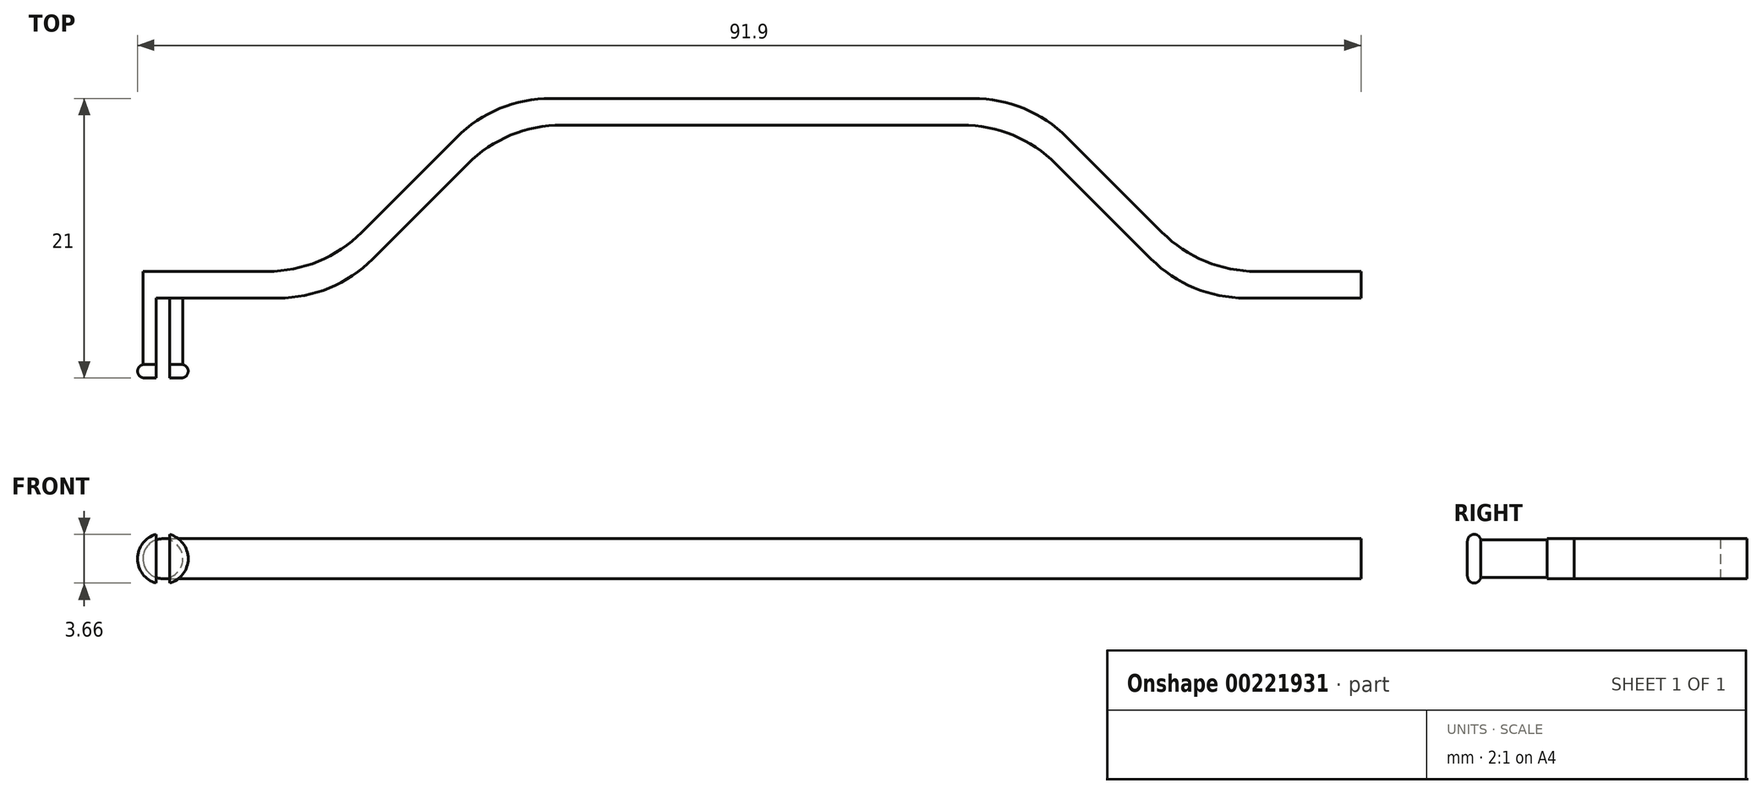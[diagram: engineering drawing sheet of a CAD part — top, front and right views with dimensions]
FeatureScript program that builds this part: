
annotation { "Feature Type Name" : "Feature", "Feature Type Description" : "" }
export const myFeature = defineFeature(function(context is Context, id is Id, definition is map)
    precondition{}
    {
        {
            var Q0;
            Q0=qCreatedBy(makeId("Top.planeOp"),FACE);
            var sketch = newSketch(context, id + "F0", { "sketchPlane" : qUnion([Q0])});
            skLineSegment(sketch, "E0.bottom", {"start": v(-45, 0) * mm, "end": v(-32.17, 0) * mm});
            skLineSegment(sketch, "E0.top", {"start": v(-45, 2) * mm, "end": v(-33, 2) * mm});
            skLineSegment(sketch, "E0.left", {"start": v(-45, 0) * mm, "end": v(-45, 2) * mm});
            skLineSegment(sketch, "E0.right", {"start": v(-32.17, 0) * mm, "end": v(-33, 2) * mm});
            skLineSegment(sketch, "E1.MirrorCS", {"start": v(32.17, 0) * mm, "end": v(33, 2) * mm});
            skLineSegment(sketch, "E2.MirrorCS", {"start": v(45, 0) * mm, "end": v(45, 2) * mm});
            skLineSegment(sketch, "E3.MirrorCS", {"start": v(45, 2) * mm, "end": v(33, 2) * mm});
            skLineSegment(sketch, "E4.MirrorCS", {"start": v(45, 0) * mm, "end": v(32.17, 0) * mm});
            skLineSegment(sketch, "E5.bottom", {"start": v(-20, 15) * mm, "end": v(0, 15) * mm});
            skLineSegment(sketch, "E5.top", {"start": v(-19.17, 13) * mm, "end": v(0, 13) * mm});
            skLineSegment(sketch, "E5.left", {"start": v(-20, 15) * mm, "end": v(-19.17, 13) * mm});
            skLineSegment(sketch, "E5.right", {"start": v(0, 15) * mm, "end": v(0, 13) * mm});
            skLineSegment(sketch, "E6.MirrorCS", {"start": v(20, 15) * mm, "end": v(19.17, 13) * mm});
            skLineSegment(sketch, "E7.MirrorCS", {"start": v(20, 15) * mm, "end": v(0, 15) * mm});
            skLineSegment(sketch, "E8.MirrorCS", {"start": v(19.17, 13) * mm, "end": v(0, 13) * mm});
            skLineSegment(sketch, "E9", {"start": v(-32.17, 0) * mm, "end": v(-19.17, 13) * mm});
            skLineSegment(sketch, "E10", {"start": v(-33, 2) * mm, "end": v(-20, 15) * mm});
            skLineSegment(sketch, "E11.MirrorCS", {"start": v(32.17, 0) * mm, "end": v(19.17, 13) * mm});
            skLineSegment(sketch, "E12.MirrorCS", {"start": v(33, 2) * mm, "end": v(20, 15) * mm});
            skLineSegment(sketch, "E13", {"start": v(-26.5, 8.5) * mm, "end": v(-25.09, 7.09) * mm, "construction": true});
            skLineSegment(sketch, "E14", {"start": v(-19.17, 13) * mm, "end": v(-19.17, 0) * mm, "construction": true});
            skSolve(sketch);
        }
        {
            var Q0;
            Q0=qSketchRegion(id+"F0",true);
            extrude(context, id + "F1", {"entities" : qUnion([Q0]), "depth" : 3 * mm});
        }
        {
            var Q0;
            Q0=makeQuery(id+"F1.opExtrude","SWEPT_EDGE",EDGE,{"disambiguationData":[OSD([sQuery(id+"F0.wireOp",EDGE,"E0.top"),sQuery(id+"F0.wireOp",EDGE,"E0.right"),sQuery(id+"F0.wireOp",EDGE,"E10")])]});
            var Q1;
            Q1=makeQuery(id+"F1.opExtrude","SWEPT_EDGE",EDGE,{"disambiguationData":[OSD([sQuery(id+"F0.wireOp",EDGE,"E5.bottom"),sQuery(id+"F0.wireOp",EDGE,"E5.left"),sQuery(id+"F0.wireOp",EDGE,"E10")])]});
            var Q2;
            Q2=makeQuery(id+"F1.opExtrude","SWEPT_EDGE",EDGE,{"disambiguationData":[OSD([sQuery(id+"F0.wireOp",EDGE,"E7.MirrorCS"),sQuery(id+"F0.wireOp",EDGE,"E6.MirrorCS"),sQuery(id+"F0.wireOp",EDGE,"E12.MirrorCS")])]});
            var Q3;
            Q3=makeQuery(id+"F1.opExtrude","SWEPT_EDGE",EDGE,{"disambiguationData":[OSD([sQuery(id+"F0.wireOp",EDGE,"E3.MirrorCS"),sQuery(id+"F0.wireOp",EDGE,"E1.MirrorCS"),sQuery(id+"F0.wireOp",EDGE,"E12.MirrorCS")])]});
            var Q4;
            Q4=makeQuery(id+"F1.opExtrude","SWEPT_EDGE",EDGE,{"disambiguationData":[OSD([sQuery(id+"F0.wireOp",EDGE,"E4.MirrorCS"),sQuery(id+"F0.wireOp",EDGE,"E11.MirrorCS"),sQuery(id+"F0.wireOp",EDGE,"E1.MirrorCS")])]});
            var Q5;
            Q5=makeQuery(id+"F1.opExtrude","SWEPT_EDGE",EDGE,{"disambiguationData":[OSD([sQuery(id+"F0.wireOp",EDGE,"E8.MirrorCS"),sQuery(id+"F0.wireOp",EDGE,"E6.MirrorCS"),sQuery(id+"F0.wireOp",EDGE,"E11.MirrorCS")])]});
            var Q6;
            Q6=makeQuery(id+"F1.opExtrude","SWEPT_EDGE",EDGE,{"disambiguationData":[OSD([sQuery(id+"F0.wireOp",EDGE,"E5.top"),sQuery(id+"F0.wireOp",EDGE,"E5.left"),sQuery(id+"F0.wireOp",EDGE,"E9")])]});
            var Q7;
            Q7=makeQuery(id+"F1.opExtrude","SWEPT_EDGE",EDGE,{"disambiguationData":[OSD([sQuery(id+"F0.wireOp",EDGE,"E0.bottom"),sQuery(id+"F0.wireOp",EDGE,"E0.right"),sQuery(id+"F0.wireOp",EDGE,"E9")])]});
            fillet(context, id + "F2", {"entities" : qUnion([Q0, Q1, Q2, Q3, Q4, Q5, Q6, Q7]), "radius" : 10 * mm, "tangentPropagation" : true, "allowEdgeOverflow" : false});
        }
        {
            var Q0;
            Q0=makeQuery(id+"F1.opExtrude","SWEPT_FACE",FACE,{"disambiguationData":[OSD([sQuery(id+"F0.wireOp",EDGE,"E0.bottom")])]});
            var sketch = newSketch(context, id + "F3", { "sketchPlane" : qUnion([Q0])});
            skCircle(sketch, "E15", {"center": v(-45, 1.5) * mm, "radius": 1.5 * mm});
            skCircle(sketch, "E16.MirrorC", {"center": v(45, 1.5) * mm, "radius": 1.5 * mm});
            skSolve(sketch);
        }
        {
            var Q0;
            {var subQ1=sQuery(id+"F0.wireOp",EDGE,"E0.bottom");var subQ2=makeQuery(id+"F1.opExtrude","SWEPT_EDGE",EDGE,{"disambiguationData":[OSD([subQ1,sQuery(id+"F0.wireOp",EDGE,"E0.left")])]});Q0=makeQuery(id+"F3.imprint","IMPRINT",FACE,{"disambiguationData":[TD([[makeQuery(id+"F3.imprint","IMPRINT",EDGE,{"derivedFrom":subQ2}),-1.0]])]});}
            var Q1;
            Q1=makeQuery(id+"F3.imprint","IMPRINT",FACE,{"disambiguationData":[TD([[makeQuery(id+"F3.imprint","IMPRINT",EDGE,{"derivedFrom":sQuery(id+"F3.wireOp",EDGE,"E16.MirrorC")}),-1.0]])]});
            var Q2;
            Q2=makeQuery(id+"F1.opExtrude","SWEPT_FACE",FACE,{"disambiguationData":[OSD([sQuery(id+"F0.wireOp",EDGE,"E0.top")])]});
            extrude(context, id + "F4", {"entities" : qUnion([Q0, Q1]), "operationType" : NewBodyOperationType.ADD, "endBound" : BoundingType.UP_TO_SURFACE, "oppositeDirection" : true, "endBoundEntityFace" : qUnion([Q2]), "depth" : 25 * mm});
        }
        {
            var Q0;
            {var subQ1=sQuery(id+"F0.wireOp",EDGE,"E0.bottom");var subQ2=makeQuery(id+"F1.opExtrude","SWEPT_EDGE",EDGE,{"disambiguationData":[OSD([subQ1,sQuery(id+"F0.wireOp",EDGE,"E0.left")])]});Q0=makeQuery(id+"F3.imprint","IMPRINT",FACE,{"disambiguationData":[TD([[makeQuery(id+"F3.imprint","IMPRINT",EDGE,{"derivedFrom":subQ2}),-1.0]])]});}
            var Q1;
            {var subQ1=sQuery(id+"F0.wireOp",EDGE,"E0.bottom");var subQ2=makeQuery(id+"F1.opExtrude","SWEPT_EDGE",EDGE,{"disambiguationData":[OSD([subQ1,sQuery(id+"F0.wireOp",EDGE,"E0.left")])]});Q1=makeQuery(id+"F3.imprint","IMPRINT",FACE,{"disambiguationData":[TD([[makeQuery(id+"F3.imprint","IMPRINT",EDGE,{"derivedFrom":subQ2}),1.0]])]});}
            var Q2;
            Q2=makeQuery(id+"F3.imprint","IMPRINT",FACE,{"disambiguationData":[TD([[makeQuery(id+"F3.imprint","IMPRINT",EDGE,{"derivedFrom":sQuery(id+"F3.wireOp",EDGE,"E16.MirrorC")}),-1.0]])]});
            extrude(context, id + "F5", {"entities" : qUnion([Q0, Q1, Q2]), "operationType" : NewBodyOperationType.ADD, "depth" : 6 * mm});
        }
        {
            var Q0;
            Q0=makeQuery(id+"F5.opExtrude","CAP_FACE",FACE,{"disambiguationData":[OSD([sQuery(id+"F3.wireOp",EDGE,"E15")])],"isStart":false});
            var sketch = newSketch(context, id + "F6", { "sketchPlane" : qUnion([Q0])});
            skCircle(sketch, "E17", {"center": v(-45, 1.5) * mm, "radius": 1.9 * mm});
            skCircle(sketch, "E18.MirrorC", {"center": v(45, 1.5) * mm, "radius": 1.9 * mm});
            skSolve(sketch);
        }
        {
            var Q0;
            Q0=makeQuery(id+"F6.imprint","IMPRINT",FACE,{"disambiguationData":[TD([[makeQuery(id+"F6.imprint","IMPRINT",EDGE,{"derivedFrom":sQuery(id+"F6.wireOp",EDGE,"E17")}),1.0]])]});
            var Q1;
            Q1=makeQuery(id+"F6.imprint","IMPRINT",FACE,{"disambiguationData":[TD([[makeQuery(id+"F6.imprint","IMPRINT",EDGE,{"derivedFrom":sQuery(id+"F6.wireOp",EDGE,"E18.MirrorC")}),-1.0]])]});
            extrude(context, id + "F7", {"entities" : qUnion([Q0, Q1]), "operationType" : NewBodyOperationType.ADD, "oppositeDirection" : true, "depth" : 1 * mm});
        }
        {
            var Q0;
            Q0=makeQuery(id+"F7.opExtrude","CAP_EDGE",EDGE,{"disambiguationData":[OSD([sQuery(id+"F6.wireOp",EDGE,"E17")])],"isStart":true});
            var Q1;
            Q1=makeQuery(id+"F7.opExtrude","CAP_EDGE",EDGE,{"disambiguationData":[OSD([sQuery(id+"F6.wireOp",EDGE,"E17")])],"isStart":false});
            var Q2;
            Q2=makeQuery(id+"F7.opExtrude","CAP_EDGE",EDGE,{"disambiguationData":[OSD([sQuery(id+"F6.wireOp",EDGE,"E18.MirrorC")])],"isStart":false});
            var Q3;
            Q3=makeQuery(id+"F7.opExtrude","CAP_EDGE",EDGE,{"disambiguationData":[OSD([sQuery(id+"F6.wireOp",EDGE,"E18.MirrorC")])],"isStart":true});
            fillet(context, id + "F8", {"entities" : qUnion([Q0, Q1, Q2, Q3]), "radius" : 0.5 * mm, "tangentPropagation" : true, "allowEdgeOverflow" : false});
        }
        {
            var Q0;
            {var subQ0=sQuery(id+"F3.wireOp",EDGE,"E15");Q0=makeQuery(id+"F7.boolean.opBoolean","MERGE",FACE,{"derivedFrom":[makeQuery(id+"F5.opExtrude","CAP_FACE",FACE,{"disambiguationData":[OSD([subQ0])],"isStart":false}),makeQuery(id+"F7.opExtrude","CAP_FACE",FACE,{"disambiguationData":[OSD([subQ0,sQuery(id+"F6.wireOp",EDGE,"E17")])],"isStart":true})]});}
            var sketch = newSketch(context, id + "F9", { "sketchPlane" : qUnion([Q0])});
            skLineSegment(sketch, "E19.bottom", {"start": v(-45.5, -3.84) * mm, "end": v(-44.5, -3.84) * mm});
            skLineSegment(sketch, "E19.top", {"start": v(-45.5, 6.84) * mm, "end": v(-44.5, 6.84) * mm});
            skLineSegment(sketch, "E19.left", {"start": v(-45.5, -3.84) * mm, "end": v(-45.5, 6.84) * mm});
            skLineSegment(sketch, "E19.right", {"start": v(-44.5, -3.84) * mm, "end": v(-44.5, 6.84) * mm});
            skPoint(sketch, "E19.middle", {"position": v(-45, 1.5) * mm});
            skLineSegment(sketch, "E20.bottom", {"start": v(-57.96, 3.4) * mm, "end": v(-50.7, 3.4) * mm});
            skLineSegment(sketch, "E20.top", {"start": v(-57.96, 2.9) * mm, "end": v(-50.7, 2.9) * mm});
            skLineSegment(sketch, "E20.left", {"start": v(-57.96, 3.4) * mm, "end": v(-57.96, 2.9) * mm});
            skLineSegment(sketch, "E20.right", {"start": v(-50.7, 3.4) * mm, "end": v(-50.7, 2.9) * mm});
            skLineSegment(sketch, "E21.bottom", {"start": v(-57.67, -0.4) * mm, "end": v(-50.7, -0.4) * mm});
            skLineSegment(sketch, "E21.top", {"start": v(-57.67, 0.1) * mm, "end": v(-50.7, 0.1) * mm});
            skLineSegment(sketch, "E21.left", {"start": v(-57.67, -0.4) * mm, "end": v(-57.67, 0.1) * mm});
            skLineSegment(sketch, "E21.right", {"start": v(-50.7, -0.4) * mm, "end": v(-50.7, 0.1) * mm});
            skLineSegment(sketch, "E22.MirrorCS", {"start": v(57.67, -0.4) * mm, "end": v(57.67, 0.1) * mm});
            skLineSegment(sketch, "E23.MirrorCS", {"start": v(50.7, 3.4) * mm, "end": v(50.7, 2.9) * mm});
            skLineSegment(sketch, "E24.MirrorCS", {"start": v(45.5, -3.84) * mm, "end": v(44.5, -3.84) * mm});
            skLineSegment(sketch, "E25.MirrorCS", {"start": v(57.96, 3.4) * mm, "end": v(57.96, 2.9) * mm});
            skLineSegment(sketch, "E26.MirrorCS", {"start": v(50.7, -0.4) * mm, "end": v(50.7, 0.1) * mm});
            skLineSegment(sketch, "E27.MirrorCS", {"start": v(45.5, 6.84) * mm, "end": v(44.5, 6.84) * mm});
            skLineSegment(sketch, "E28.MirrorCS", {"start": v(57.96, 2.9) * mm, "end": v(50.7, 2.9) * mm});
            skPoint(sketch, "E29.MirrorP", {"position": v(45, 1.5) * mm});
            skLineSegment(sketch, "E30.MirrorCS", {"start": v(57.67, 0.1) * mm, "end": v(50.7, 0.1) * mm});
            skLineSegment(sketch, "E31.MirrorCS", {"start": v(57.67, -0.4) * mm, "end": v(50.7, -0.4) * mm});
            skLineSegment(sketch, "E32.MirrorCS", {"start": v(57.96, 3.4) * mm, "end": v(50.7, 3.4) * mm});
            skLineSegment(sketch, "E33.MirrorCS", {"start": v(45.5, -3.84) * mm, "end": v(45.5, 6.84) * mm});
            skLineSegment(sketch, "E34.MirrorCS", {"start": v(44.5, -3.84) * mm, "end": v(44.5, 6.84) * mm});
            skSolve(sketch);
        }
        {
            var Q0;
            Q0=qSketchRegion(id+"F9",true);
            var Q1;
            {var subQ0=sQuery(id+"F0.wireOp",EDGE,"E0.bottom");Q1=makeQuery(id+"F4.boolean.opBoolean","MERGE",FACE,{"derivedFrom":[makeQuery(id+"F1.opExtrude","SWEPT_FACE",FACE,{"disambiguationData":[OSD([subQ0])]}),makeQuery(id+"F4.opExtrude","CAP_FACE",FACE,{"disambiguationData":[OSD([subQ0,sQuery(id+"F0.wireOp",EDGE,"E0.left"),sQuery(id+"F3.wireOp",EDGE,"E15")])],"isStart":true})]});}
            extrude(context, id + "F10", {"entities" : qUnion([Q0]), "operationType" : NewBodyOperationType.REMOVE, "endBound" : BoundingType.UP_TO_SURFACE, "oppositeDirection" : true, "endBoundEntityFace" : qUnion([Q1]), "depth" : 25 * mm});
        }
    });
